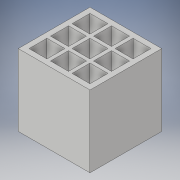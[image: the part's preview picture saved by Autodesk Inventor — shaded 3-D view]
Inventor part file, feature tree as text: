
AUTODESK INVENTOR PART (.ipt)
format: ipt  version: 2019 (Build 230136000, 136)  size: 142,848 bytes
history: native  units: in
note: dims shown in document units (in); Inventor stores cm internally (conversion verified against a paired STEP export)
features: extrude x2, sketch x2, projected_geometry x1
ambient origin geometry x8: Origin, YZ Plane, XZ Plane, XY Plane, X Axis, Y Axis, Z Axis, Center Point
bodies: Solid1 (feature_tree)
feature tree (5):
  extrude  "Extrusion1"  Depth=2.0in
  extrude  "Extrusion2"  Depth=0.5in
  sketch  "Sketch1"  dims[d0=2.0in d1=2.0in]
  sketch  "Sketch2"  dims[d2=2.0in d3=0.0in d4=0.5in d5=0.5in d6=0.15in d7=0.15in d8=1.1811in d10=0.6in d11=1.1811in d13=0.6in d16=1.0in d17=0.0in]
  projected_geometry  "Projected Loop1"
